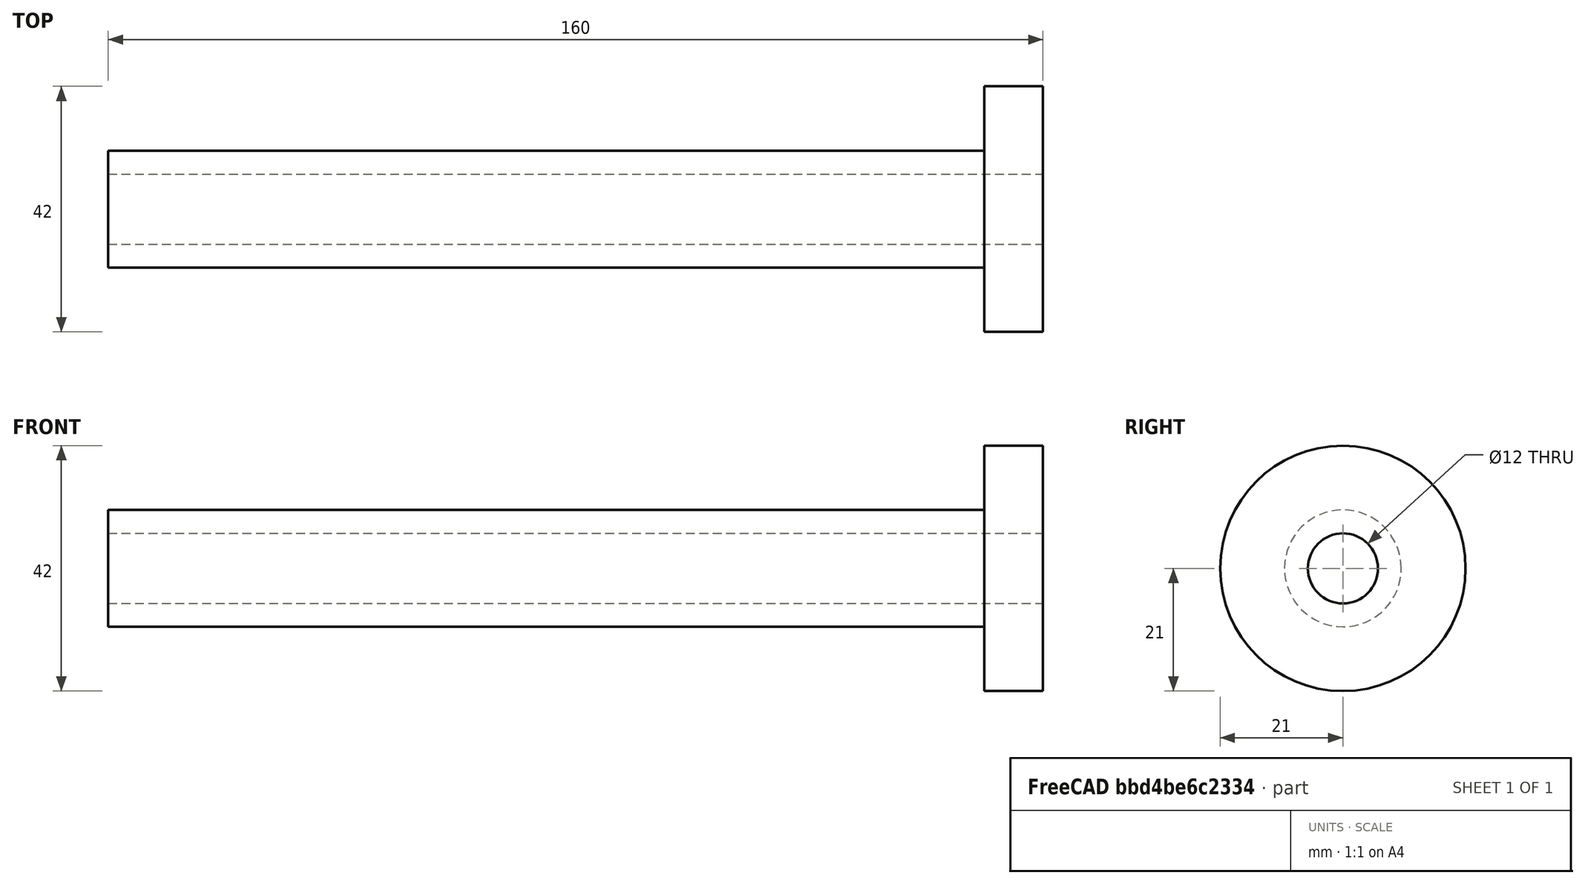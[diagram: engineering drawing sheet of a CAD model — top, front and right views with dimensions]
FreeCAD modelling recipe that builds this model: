
FCSTD DOCUMENT  (FreeCAD 0.20RUnknown)
Label: peca3
License: All rights reserved
LicenseURL: http://en.wikipedia.org/wiki/All_rights_reserved
objects: Sketcher::SketchObject×1, PartDesign::Revolution×1, PartDesign::Body×1
note: 4 computed .brp shape members not serialized (recipe doc carries the construction recipe); baked Part::Feature solids carry a one-line shape summary decoded from their .brp

FEATURE [Sketcher::SketchObject] Sketch001
  FullyConstrained = true
  MapMode = 5
  Support = -> [XY_Plane]
  sketch-geometry (6):
    g0: LineSegment StartX=-80 StartY=6 StartZ=0 EndX=80 EndY=6 EndZ=0
    g1: LineSegment StartX=80 StartY=6 StartZ=0 EndX=80 EndY=21 EndZ=0
    g2: LineSegment StartX=80 StartY=21 StartZ=0 EndX=70 EndY=21 EndZ=0
    g3: LineSegment StartX=70 StartY=21 StartZ=0 EndX=70 EndY=10 EndZ=0
    g4: LineSegment StartX=70 StartY=10 StartZ=0 EndX=-80 EndY=10 EndZ=0
    g5: LineSegment StartX=-80 StartY=10 StartZ=0 EndX=-80 EndY=6 EndZ=0
  constraints (17):
    c: Coincident(g0,g1)
    c: Vertical(g1)
    c: Coincident(g1,g2)
    c: Horizontal(g2)
    c: Coincident(g2,g3)
    c: Coincident(g3,g4)
    c: Horizontal(g4)
    c: Coincident(g4,g5)
    c: Coincident(g5,g0)
    c: Vertical(g5)
    c: Vertical(g3)
    c: DistanceX(g4,g3) = 150
    c: DistanceY(g0,g1) = 15
    c: DistanceY(g-1,g4) = 10
    c: DistanceY(g-1,g0) = 6
    c: Symmetric(g0,g0,g-2)
    c: DistanceX(g2,g1) = 10
FEATURE [PartDesign::Revolution] Revolution
  Angle = 360
  Axis = (1,0,0)
  Base = (0,0,0)
  Profile = -> Sketch001
  ReferenceAxis = -> Sketch001 [H_Axis]
FEATURE [PartDesign::Body] Body
  Group = -> [Sketch001,Revolution]
  Origin = -> Origin
  Tip = -> Revolution
